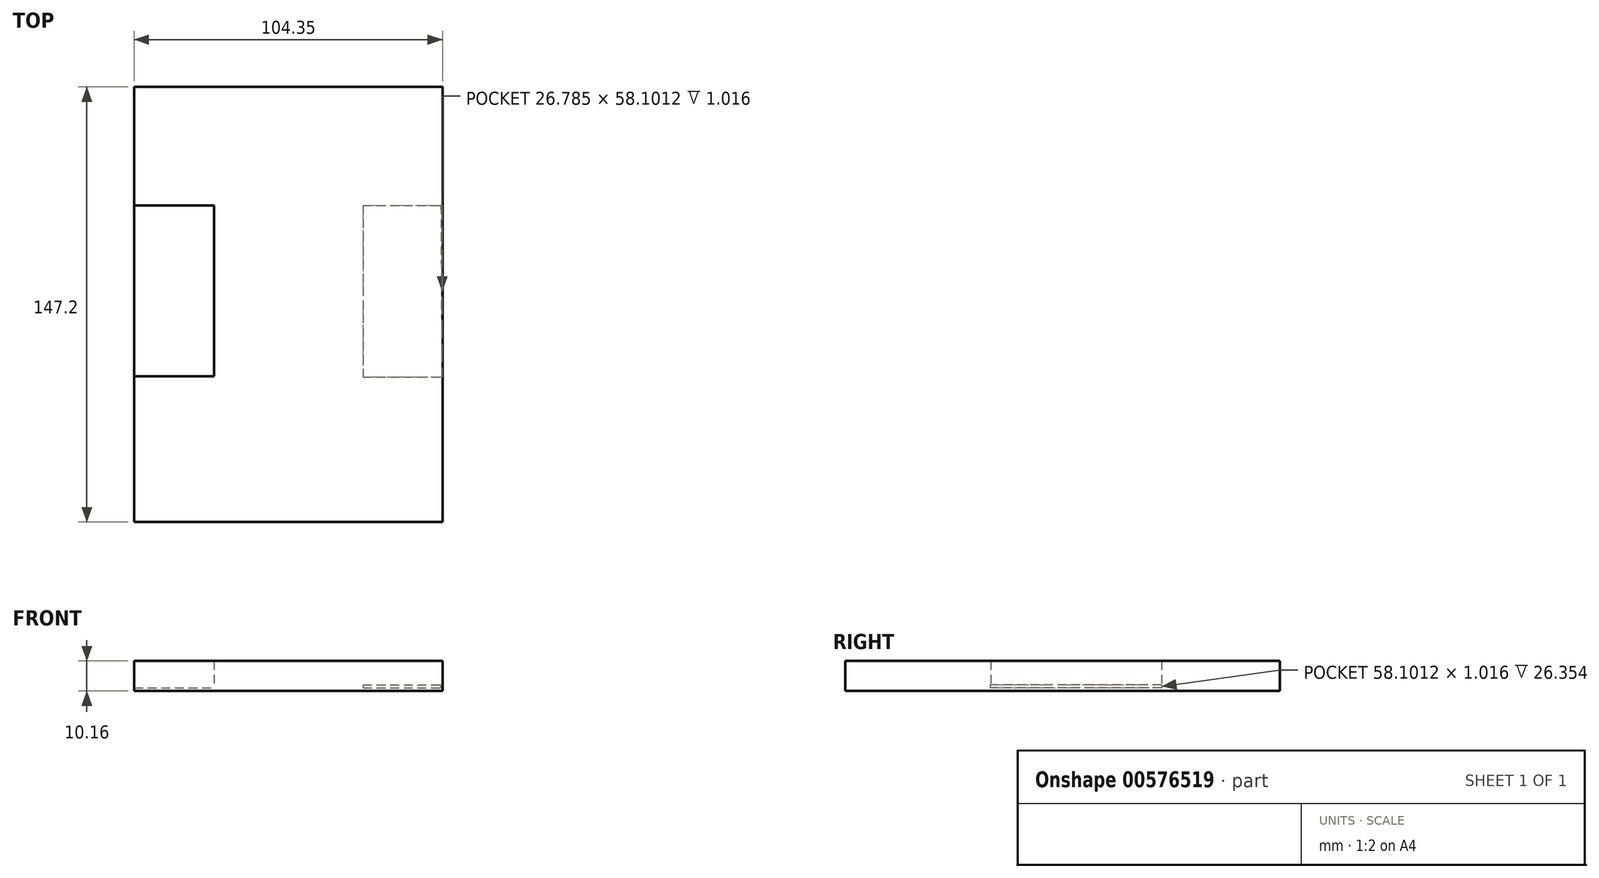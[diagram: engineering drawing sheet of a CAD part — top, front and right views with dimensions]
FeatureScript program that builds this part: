
annotation { "Feature Type Name" : "Feature", "Feature Type Description" : "" }
export const myFeature = defineFeature(function(context is Context, id is Id, definition is map)
    precondition{}
    {
        {
            var Q0;
            Q0=qCreatedBy(makeId("Top.planeOp"),FACE);
            var sketch = newSketch(context, id + "F0", { "sketchPlane" : qUnion([Q0])});
            skLineSegment(sketch, "E0.bottom", {"start": v(-44.01, 73.3) * mm, "end": v(60.34, 73.3) * mm});
            skLineSegment(sketch, "E0.top", {"start": v(-44.01, -73.89) * mm, "end": v(60.34, -73.89) * mm});
            skLineSegment(sketch, "E0.left", {"start": v(-44.01, 73.3) * mm, "end": v(-44.01, -73.89) * mm});
            skLineSegment(sketch, "E0.right", {"start": v(60.34, 73.3) * mm, "end": v(60.34, -73.89) * mm});
            skSolve(sketch);
        }
        {
            var Q0;
            Q0=makeQuery(id+"F0.imprint","IMPRINT",FACE,{"disambiguationData":[TD([[makeQuery(id+"F0.imprint","IMPRINT",EDGE,{"derivedFrom":sQuery(id+"F0.wireOp",EDGE,"E0.bottom")}),-1.0]])]});
            var sketch = newSketch(context, id + "F1", { "sketchPlane" : qUnion([Q0])});
            skLineSegment(sketch, "E1", {"start": v(-44.35, 33.23) * mm, "end": v(59.78, 33.23) * mm});
            skLineSegment(sketch, "E2", {"start": v(-17.03, 33.23) * mm, "end": v(-17.03, -24.62) * mm});
            skLineSegment(sketch, "E3", {"start": v(-17.03, -24.62) * mm, "end": v(-44.03, -24.62) * mm});
            skLineSegment(sketch, "E4", {"start": v(33.43, 33.23) * mm, "end": v(33.43, -24.87) * mm});
            skLineSegment(sketch, "E5", {"start": v(33.43, -24.87) * mm, "end": v(60.21, -24.87) * mm});
            skLineSegment(sketch, "E6", {"start": v(-44.03, -24.62) * mm, "end": v(-44.35, 33.23) * mm});
            skLineSegment(sketch, "E7", {"start": v(59.78, 33.23) * mm, "end": v(60.21, -24.87) * mm});
            skSolve(sketch);
        }
        {
            var Q0;
            {var subQ4=sQuery(id+"F1.wireOp",EDGE,"E2");Q0=makeQuery(id+"F1.imprint","IMPRINT",FACE,{"disambiguationData":[TD([[makeQuery(id+"F1.imprint","IMPRINT",EDGE,{"derivedFrom":subQ4}),1.0]])]});}
            extrude(context, id + "F2", {"entities" : qUnion([Q0]), "depth" : 9.14 * mm, "offsetDistance" : 25.4 * mm});
        }
        {
            var Q0;
            Q0=makeQuery(id+"F0.imprint","IMPRINT",FACE,{"disambiguationData":[TD([[makeQuery(id+"F0.imprint","IMPRINT",EDGE,{"derivedFrom":sQuery(id+"F0.wireOp",EDGE,"E0.bottom")}),-1.0]])]});
            var Q1;
            Q1=makeQuery(id+"F2.opExtrude","CAP_FACE",FACE,{"disambiguationData":[OSD([sQuery(id+"F0.wireOp",EDGE,"E0.bottom"),sQuery(id+"F0.wireOp",EDGE,"E0.top"),sQuery(id+"F0.wireOp",EDGE,"E0.left"),sQuery(id+"F0.wireOp",EDGE,"E0.right"),sQuery(id+"F1.wireOp",EDGE,"E1"),sQuery(id+"F1.wireOp",EDGE,"E2"),sQuery(id+"F1.wireOp",EDGE,"E3"),sQuery(id+"F1.wireOp",EDGE,"E4"),sQuery(id+"F1.wireOp",EDGE,"E5"),sQuery(id+"F1.wireOp",EDGE,"E7")])],"isStart":false});
            extrude(context, id + "F3", {"entities" : qUnion([Q0, Q1]), "operationType" : NewBodyOperationType.ADD, "oppositeDirection" : true, "depth" : 1.02 * mm, "offsetDistance" : 25.4 * mm});
        }
        {
            var Q0;
            Q0=makeQuery(id+"F2.opExtrude","CAP_FACE",FACE,{"disambiguationData":[OSD([sQuery(id+"F0.wireOp",EDGE,"E0.bottom"),sQuery(id+"F0.wireOp",EDGE,"E0.top"),sQuery(id+"F0.wireOp",EDGE,"E0.left"),sQuery(id+"F0.wireOp",EDGE,"E0.right"),sQuery(id+"F1.wireOp",EDGE,"E1"),sQuery(id+"F1.wireOp",EDGE,"E2"),sQuery(id+"F1.wireOp",EDGE,"E3"),sQuery(id+"F1.wireOp",EDGE,"E4"),sQuery(id+"F1.wireOp",EDGE,"E5"),sQuery(id+"F1.wireOp",EDGE,"E7")])],"isStart":false});
            var sketch = newSketch(context, id + "F4", { "sketchPlane" : qUnion([Q0])});
            skLineSegment(sketch, "E8", {"start": v(-17.03, 33.23) * mm, "end": v(33.43, 33.23) * mm});
            skSolve(sketch);
        }
        {
            var Q0;
            {var subQ2=sQuery(id+"F1.wireOp",EDGE,"E4");Q0=makeQuery(id+"F4.imprint","IMPRINT",FACE,{"disambiguationData":[TD([[makeQuery(id+"F4.imprint","IMPRINT",EDGE,{"derivedFrom":makeQuery(id+"F2.opExtrude","CAP_EDGE",EDGE,{"disambiguationData":[OSD([subQ2])],"isStart":false})}),1.0]])]});}
            extrude(context, id + "F5", {"entities" : qUnion([Q0]), "operationType" : NewBodyOperationType.ADD, "oppositeDirection" : true, "depth" : 8.13 * mm, "offsetDistance" : 25.4 * mm});
        }
    });
